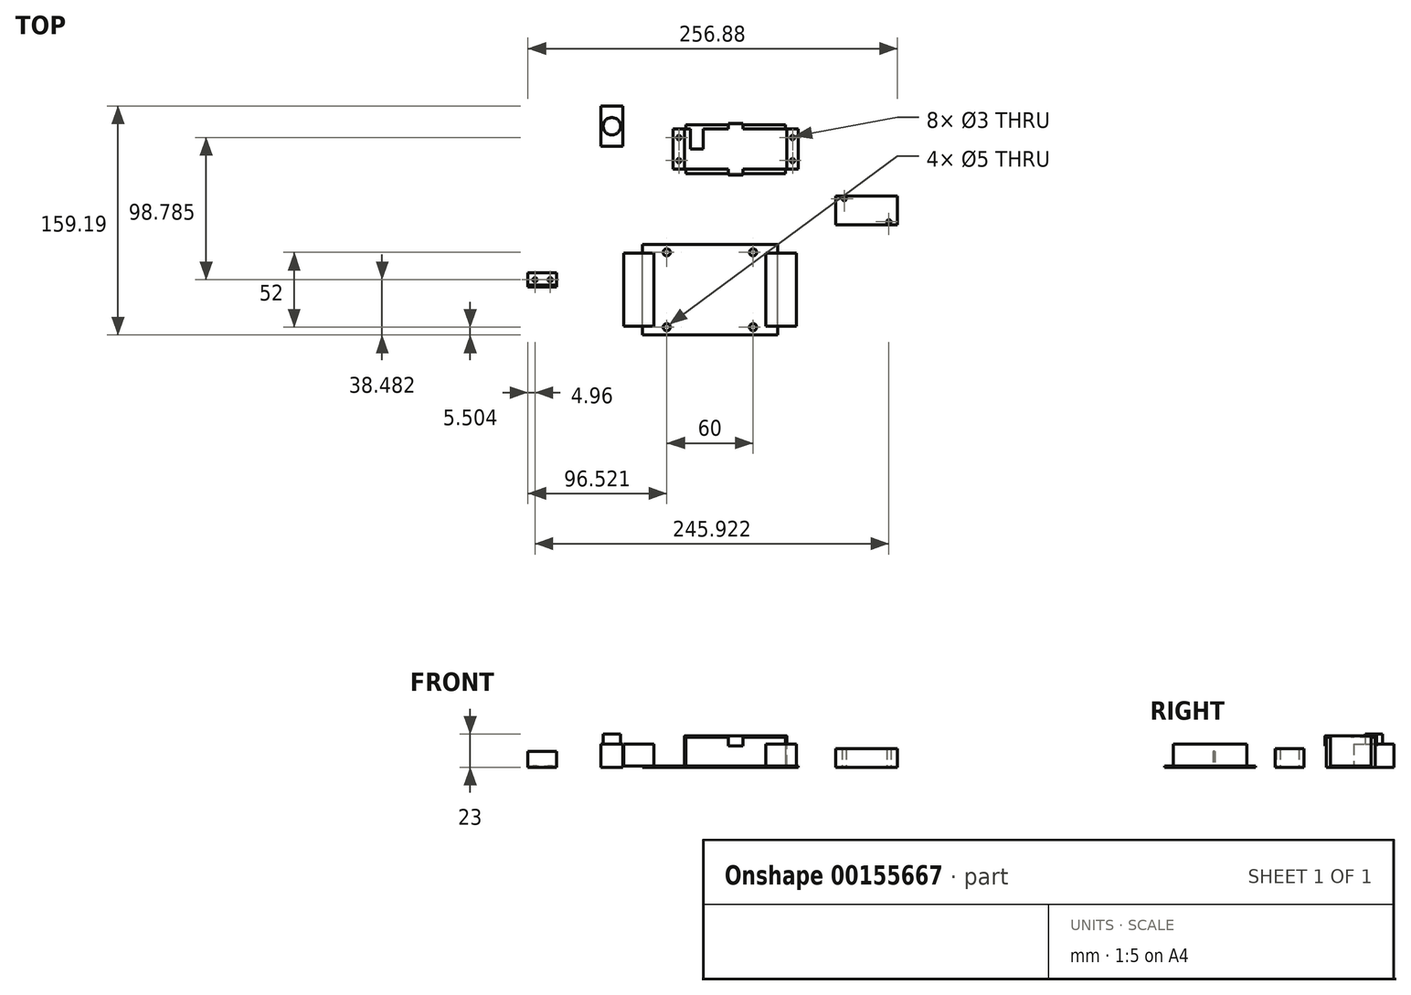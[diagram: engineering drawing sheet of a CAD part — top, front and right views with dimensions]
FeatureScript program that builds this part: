
annotation { "Feature Type Name" : "Feature", "Feature Type Description" : "" }
export const myFeature = defineFeature(function(context is Context, id is Id, definition is map)
    precondition{}
    {
        {
            var Q0;
            Q0=qCreatedBy(makeId("Top.planeOp"),FACE);
            var sketch = newSketch(context, id + "F0", { "sketchPlane" : qUnion([Q0])});
            skLineSegment(sketch, "E0.bottom", {"start": v(70.02, 20.44) * mm, "end": v(1.02, 20.44) * mm});
            skLineSegment(sketch, "E0.top", {"start": v(70.02, 54.44) * mm, "end": v(1.02, 54.44) * mm});
            skLineSegment(sketch, "E0.left", {"start": v(70.02, 20.44) * mm, "end": v(70.02, 54.44) * mm});
            skLineSegment(sketch, "E0.right", {"start": v(1.02, 20.44) * mm, "end": v(1.02, 54.44) * mm});
            skPoint(sketch, "E0.middle", {"position": v(35.52, 37.44) * mm});
            skSolve(sketch);
        }
        {
            var Q0;
            Q0 = qSketchRegion(id + "F0", true);
            extrude(context, id + "F1", {"entities" : qUnion([Q0]), "depth" : 21 * mm});
        }
        {
            var Q0;
            Q0=qCreatedBy(makeId("Top.planeOp"),FACE);
            var sketch = newSketch(context, id + "F2", { "sketchPlane" : qUnion([Q0])});
            skLineSegment(sketch, "E1.bottom", {"start": v(64.6, -91.83) * mm, "end": v(-29.4, -91.83) * mm});
            skLineSegment(sketch, "E1.top", {"start": v(64.6, -28.83) * mm, "end": v(-29.4, -28.83) * mm});
            skLineSegment(sketch, "E1.left", {"start": v(64.6, -91.83) * mm, "end": v(64.6, -28.83) * mm});
            skLineSegment(sketch, "E1.right", {"start": v(-29.4, -91.83) * mm, "end": v(-29.4, -28.83) * mm});
            skPoint(sketch, "E1.middle", {"position": v(17.6, -60.33) * mm});
            skCircle(sketch, "E2", {"center": v(-12.4, -86.33) * mm, "radius": 2.5 * mm});
            skCircle(sketch, "E3", {"center": v(-12.4, -34.33) * mm, "radius": 2.5 * mm});
            skCircle(sketch, "E4", {"center": v(47.6, -34.33) * mm, "radius": 2.5 * mm});
            skCircle(sketch, "E5", {"center": v(47.6, -86.33) * mm, "radius": 2.5 * mm});
            skSolve(sketch);
        }
        {
            var Q0;
            Q0 = qSketchRegion(id + "F2", true);
            extrude(context, id + "F3", {"entities" : qUnion([Q0]), "depth" : 1 * mm});
        }
        {
            var Q0;
            Q0=makeQuery(id+"F3.opExtrude","CAP_FACE",FACE,{"disambiguationData":[OSD([sQuery(id+"F2.wireOp",EDGE,"E1.bottom"),sQuery(id+"F2.wireOp",EDGE,"E1.top"),sQuery(id+"F2.wireOp",EDGE,"E1.left"),sQuery(id+"F2.wireOp",EDGE,"E1.right")])],"isStart":false});
            var sketch = newSketch(context, id + "F4", { "sketchPlane" : qUnion([Q0])});
            skLineSegment(sketch, "E6.bottom", {"start": v(-21.4, -85.83) * mm, "end": v(-42.4, -85.83) * mm});
            skLineSegment(sketch, "E6.top", {"start": v(-21.4, -34.83) * mm, "end": v(-42.4, -34.83) * mm});
            skLineSegment(sketch, "E6.left", {"start": v(-21.4, -85.83) * mm, "end": v(-21.4, -34.83) * mm});
            skLineSegment(sketch, "E6.right", {"start": v(-42.4, -85.83) * mm, "end": v(-42.4, -34.83) * mm});
            skPoint(sketch, "E6.middle", {"position": v(-31.9, -60.33) * mm});
            skPoint(sketch, "E7", {"position": v(-29.4, -60.33) * mm});
            skLineSegment(sketch, "E8.bottom", {"start": v(77.6, -85.83) * mm, "end": v(56.6, -85.83) * mm});
            skLineSegment(sketch, "E8.top", {"start": v(77.6, -34.83) * mm, "end": v(56.6, -34.83) * mm});
            skLineSegment(sketch, "E8.left", {"start": v(77.6, -85.83) * mm, "end": v(77.6, -34.83) * mm});
            skLineSegment(sketch, "E8.right", {"start": v(56.6, -85.83) * mm, "end": v(56.6, -34.83) * mm});
            skPoint(sketch, "E8.middle", {"position": v(67.1, -60.33) * mm});
            skPoint(sketch, "E8.middle.positionSnap0", {"position": v(64.6, -60.33) * mm});
            skPoint(sketch, "E8.centerSnap0", {"position": v(64.6, -60.33) * mm});
            skSolve(sketch);
        }
        {
            var Q0;
            Q0 = qSketchRegion(id + "F4", true);
            extrude(context, id + "F5", {"entities" : qUnion([Q0]), "operationType" : NewBodyOperationType.ADD, "depth" : 15 * mm});
        }
        {
            var Q0;
            Q0=qCreatedBy(makeId("Top.planeOp"),FACE);
            var sketch = newSketch(context, id + "F6", { "sketchPlane" : qUnion([Q0])});
            skLineSegment(sketch, "E9.bottom", {"start": v(147.95, -15.06) * mm, "end": v(104.95, -15.06) * mm});
            skLineSegment(sketch, "E9.top", {"start": v(147.95, 4.94) * mm, "end": v(104.95, 4.94) * mm});
            skLineSegment(sketch, "E9.left", {"start": v(147.95, -15.06) * mm, "end": v(147.95, 4.94) * mm});
            skLineSegment(sketch, "E9.right", {"start": v(104.95, -15.06) * mm, "end": v(104.95, 4.94) * mm});
            skPoint(sketch, "E9.middle", {"position": v(126.45, -5.06) * mm});
            skCircle(sketch, "E10", {"center": v(141.95, -13.06) * mm, "radius": 1.5 * mm});
            skCircle(sketch, "E11", {"center": v(110.95, 2.94) * mm, "radius": 1.5 * mm});
            skSolve(sketch);
        }
        {
            var Q0;
            Q0 = qSketchRegion(id + "F6", true);
            extrude(context, id + "F7", {"entities" : qUnion([Q0]), "depth" : 13 * mm});
        }
        {
            var Q0;
            Q0=qCreatedBy(makeId("Top.planeOp"),FACE);
            var sketch = newSketch(context, id + "F8", { "sketchPlane" : qUnion([Q0])});
            skLineSegment(sketch, "E12.bottom", {"start": v(-43.03, 39.36) * mm, "end": v(-58.03, 39.36) * mm});
            skLineSegment(sketch, "E12.top", {"start": v(-43.03, 67.36) * mm, "end": v(-58.03, 67.36) * mm});
            skLineSegment(sketch, "E12.left", {"start": v(-43.03, 39.36) * mm, "end": v(-43.03, 67.36) * mm});
            skLineSegment(sketch, "E12.right", {"start": v(-58.03, 39.36) * mm, "end": v(-58.03, 67.36) * mm});
            skPoint(sketch, "E12.middle", {"position": v(-50.53, 53.36) * mm});
            skSolve(sketch);
        }
        {
            var Q0;
            Q0 = qSketchRegion(id + "F8", true);
            extrude(context, id + "F9", {"entities" : qUnion([Q0]), "depth" : 16 * mm});
        }
        {
            var Q0;
            Q0=makeQuery(id+"F9.opExtrude","CAP_FACE",FACE,{"disambiguationData":[OSD([sQuery(id+"F8.wireOp",EDGE,"E12.bottom"),sQuery(id+"F8.wireOp",EDGE,"E12.top"),sQuery(id+"F8.wireOp",EDGE,"E12.left"),sQuery(id+"F8.wireOp",EDGE,"E12.right")])],"isStart":false});
            var sketch = newSketch(context, id + "F10", { "sketchPlane" : qUnion([Q0])});
            skCircle(sketch, "E13", {"center": v(-50.53, 53.36) * mm, "radius": 6 * mm});
            skSolve(sketch);
        }
        {
            var Q0;
            Q0 = qSketchRegion(id + "F10", true);
            extrude(context, id + "F11", {"entities" : qUnion([Q0]), "operationType" : NewBodyOperationType.ADD, "depth" : 7 * mm});
        }
        {
            var Q0;
            Q0=qCreatedBy(makeId("Top.planeOp"),FACE);
            var sketch = newSketch(context, id + "F12", { "sketchPlane" : qUnion([Q0])});
            skLineSegment(sketch, "E14.bottom", {"start": v(-108.93, -48.42) * mm, "end": v(-88.93, -48.42) * mm});
            skLineSegment(sketch, "E14.top", {"start": v(-108.93, -58.42) * mm, "end": v(-88.93, -58.42) * mm});
            skLineSegment(sketch, "E14.left", {"start": v(-108.93, -48.42) * mm, "end": v(-108.93, -58.42) * mm});
            skLineSegment(sketch, "E14.right", {"start": v(-88.93, -48.42) * mm, "end": v(-88.93, -58.42) * mm});
            skCircle(sketch, "E15", {"center": v(-103.97, -53.35) * mm, "radius": 1.5 * mm});
            skCircle(sketch, "E16", {"center": v(-93.43, -53.35) * mm, "radius": 1.5 * mm});
            skSolve(sketch);
        }
        {
            var Q0;
            Q0 = qSketchRegion(id + "F12", true);
            extrude(context, id + "F13", {"entities" : qUnion([Q0]), "depth" : 1 * mm});
        }
        {
            var Q0;
            Q0=makeQuery(id+"F13.opExtrude","CAP_FACE",FACE,{"disambiguationData":[OSD([sQuery(id+"F12.wireOp",EDGE,"E14.bottom"),sQuery(id+"F12.wireOp",EDGE,"E14.top"),sQuery(id+"F12.wireOp",EDGE,"E14.left"),sQuery(id+"F12.wireOp",EDGE,"E14.right"),sQuery(id+"F12.wireOp",EDGE,"E15"),sQuery(id+"F12.wireOp",EDGE,"E16")])],"isStart":false});
            var sketch = newSketch(context, id + "F14", { "sketchPlane" : qUnion([Q0])});
            skLineSegment(sketch, "E17.bottom", {"start": v(-108.93, -58.42) * mm, "end": v(-88.93, -58.42) * mm});
            skLineSegment(sketch, "E17.top", {"start": v(-108.93, -57.15) * mm, "end": v(-88.93, -57.15) * mm});
            skLineSegment(sketch, "E17.left", {"start": v(-108.93, -58.42) * mm, "end": v(-108.93, -57.15) * mm});
            skLineSegment(sketch, "E17.right", {"start": v(-88.93, -58.42) * mm, "end": v(-88.93, -57.15) * mm});
            skSolve(sketch);
        }
        {
            var Q0;
            Q0 = qSketchRegion(id + "F14", true);
            extrude(context, id + "F15", {"entities" : qUnion([Q0]), "operationType" : NewBodyOperationType.ADD, "depth" : 10 * mm});
        }
        {
            var Q0;
            Q0=makeQuery(id+"F1.opExtrude","CAP_FACE",FACE,{"disambiguationData":[OSD([sQuery(id+"F0.wireOp",EDGE,"E0.bottom"),sQuery(id+"F0.wireOp",EDGE,"E0.top"),sQuery(id+"F0.wireOp",EDGE,"E0.left"),sQuery(id+"F0.wireOp",EDGE,"E0.right")])],"isStart":false});
            var sketch = newSketch(context, id + "F16", { "sketchPlane" : qUnion([Q0])});
            skLineSegment(sketch, "E18.bottom", {"start": v(1.02, 51.44) * mm, "end": v(4.02, 51.44) * mm});
            skLineSegment(sketch, "E18.top", {"start": v(1.02, 23.44) * mm, "end": v(70.02, 23.44) * mm});
            skLineSegment(sketch, "E18.left", {"start": v(1.02, 51.44) * mm, "end": v(1.02, 23.44) * mm});
            skLineSegment(sketch, "E18.right", {"start": v(70.02, 51.44) * mm, "end": v(70.02, 23.44) * mm});
            skLineSegment(sketch, "E19.top", {"start": v(4.02, 37.44) * mm, "end": v(13.02, 37.44) * mm});
            skLineSegment(sketch, "E19.left", {"start": v(4.02, 51.44) * mm, "end": v(4.02, 37.44) * mm});
            skLineSegment(sketch, "E19.right", {"start": v(13.02, 51.44) * mm, "end": v(13.02, 37.44) * mm});
            skLineSegment(sketch, "E20.trimOffspring", {"start": v(13.02, 51.44) * mm, "end": v(70.02, 51.44) * mm});
            skLineSegment(sketch, "E21.bottom", {"start": v(30.52, 23.44) * mm, "end": v(40.52, 23.44) * mm});
            skLineSegment(sketch, "E21.top", {"start": v(30.52, 20.44) * mm, "end": v(40.52, 20.44) * mm});
            skLineSegment(sketch, "E21.left", {"start": v(30.52, 23.44) * mm, "end": v(30.52, 20.44) * mm});
            skLineSegment(sketch, "E21.right", {"start": v(40.52, 23.44) * mm, "end": v(40.52, 20.44) * mm});
            skLineSegment(sketch, "E22.bottom", {"start": v(30.52, 51.44) * mm, "end": v(40.52, 51.44) * mm});
            skLineSegment(sketch, "E22.top", {"start": v(30.52, 54.44) * mm, "end": v(40.52, 54.44) * mm});
            skLineSegment(sketch, "E22.left", {"start": v(30.52, 51.44) * mm, "end": v(30.52, 54.44) * mm});
            skLineSegment(sketch, "E22.right", {"start": v(40.52, 51.44) * mm, "end": v(40.52, 54.44) * mm});
            skSolve(sketch);
        }
        {
            var Q0;
            Q0 = qSketchRegion(id + "F16", true);
            extrude(context, id + "F17", {"entities" : qUnion([Q0]), "depth" : 1 * mm});
        }
        {
            var Q0;
            Q0=makeQuery(id+"F17.opExtrude","CAP_FACE",FACE,{"disambiguationData":[OSD([sQuery(id+"F16.wireOp",EDGE,"E18.bottom"),sQuery(id+"F16.wireOp",EDGE,"E18.top"),sQuery(id+"F16.wireOp",EDGE,"E18.left"),sQuery(id+"F16.wireOp",EDGE,"E18.right")])],"isStart":false});
            var sketch = newSketch(context, id + "F18", { "sketchPlane" : qUnion([Q0])});
            skLineSegment(sketch, "E23.bottom", {"start": v(1.02, 51.44) * mm, "end": v(0.02, 51.44) * mm});
            skLineSegment(sketch, "E23.top", {"start": v(1.02, 23.44) * mm, "end": v(0.02, 23.44) * mm});
            skLineSegment(sketch, "E23.left", {"start": v(1.02, 51.44) * mm, "end": v(1.02, 23.44) * mm});
            skLineSegment(sketch, "E23.right", {"start": v(0.02, 51.44) * mm, "end": v(0.02, 23.44) * mm});
            skLineSegment(sketch, "E24.bottom", {"start": v(70.02, 51.44) * mm, "end": v(71.02, 51.44) * mm});
            skLineSegment(sketch, "E24.top", {"start": v(70.02, 23.44) * mm, "end": v(71.02, 23.44) * mm});
            skLineSegment(sketch, "E24.left", {"start": v(70.02, 51.44) * mm, "end": v(70.02, 23.44) * mm});
            skLineSegment(sketch, "E24.right", {"start": v(71.02, 51.44) * mm, "end": v(71.02, 23.44) * mm});
            skLineSegment(sketch, "E25.bottom", {"start": v(30.52, 20.44) * mm, "end": v(40.52, 20.44) * mm});
            skLineSegment(sketch, "E25.top", {"start": v(30.52, 19.44) * mm, "end": v(40.52, 19.44) * mm});
            skLineSegment(sketch, "E25.left", {"start": v(30.52, 20.44) * mm, "end": v(30.52, 19.44) * mm});
            skLineSegment(sketch, "E25.right", {"start": v(40.52, 20.44) * mm, "end": v(40.52, 19.44) * mm});
            skLineSegment(sketch, "E26.bottom", {"start": v(30.52, 54.44) * mm, "end": v(40.52, 54.44) * mm});
            skLineSegment(sketch, "E26.top", {"start": v(30.52, 55.44) * mm, "end": v(40.52, 55.44) * mm});
            skLineSegment(sketch, "E26.left", {"start": v(30.52, 54.44) * mm, "end": v(30.52, 55.44) * mm});
            skLineSegment(sketch, "E26.right", {"start": v(40.52, 54.44) * mm, "end": v(40.52, 55.44) * mm});
            skSolve(sketch);
        }
        {
            var Q0;
            Q0=makeQuery(id+"F18.imprint","IMPRINT",FACE,{"disambiguationData":[TD([[makeQuery(id+"F18.imprint","IMPRINT",EDGE,{"derivedFrom":sQuery(id+"F18.wireOp",EDGE,"E23.bottom")}),1.0]])]});
            var Q1;
            Q1=makeQuery(id+"F18.imprint","IMPRINT",FACE,{"disambiguationData":[TD([[makeQuery(id+"F18.imprint","IMPRINT",EDGE,{"derivedFrom":sQuery(id+"F18.wireOp",EDGE,"E24.bottom")}),-1.0]])]});
            extrude(context, id + "F19", {"entities" : qUnion([Q0, Q1]), "operationType" : NewBodyOperationType.ADD, "oppositeDirection" : true, "depth" : 22 * mm});
        }
        {
            var Q0;
            Q0=makeQuery(id+"F19.opExtrude","SWEPT_FACE",FACE,{"disambiguationData":[OSD([sQuery(id+"F18.wireOp",EDGE,"E23.right")])]});
            var sketch = newSketch(context, id + "F20", { "sketchPlane" : qUnion([Q0])});
            skLineSegment(sketch, "E27.bottom", {"start": v(-51.44, 0) * mm, "end": v(-23.44, 0) * mm});
            skLineSegment(sketch, "E27.top", {"start": v(-51.44, 1) * mm, "end": v(-23.44, 1) * mm});
            skLineSegment(sketch, "E27.left", {"start": v(-51.44, 0) * mm, "end": v(-51.44, 1) * mm});
            skLineSegment(sketch, "E27.right", {"start": v(-23.44, 0) * mm, "end": v(-23.44, 1) * mm});
            skSolve(sketch);
        }
        {
            var Q0;
            Q0 = qSketchRegion(id + "F20", true);
            extrude(context, id + "F21", {"entities" : qUnion([Q0]), "operationType" : NewBodyOperationType.ADD, "depth" : 8 * mm});
        }
        {
            var Q0;
            Q0=makeQuery(id+"F19.opExtrude","SWEPT_FACE",FACE,{"disambiguationData":[OSD([sQuery(id+"F18.wireOp",EDGE,"E24.right")])]});
            var sketch = newSketch(context, id + "F22", { "sketchPlane" : qUnion([Q0])});
            skLineSegment(sketch, "E28.bottom", {"start": v(23.44, 0) * mm, "end": v(51.44, 0) * mm});
            skLineSegment(sketch, "E28.top", {"start": v(23.44, 1) * mm, "end": v(51.44, 1) * mm});
            skLineSegment(sketch, "E28.left", {"start": v(23.44, 0) * mm, "end": v(23.44, 1) * mm});
            skLineSegment(sketch, "E28.right", {"start": v(51.44, 0) * mm, "end": v(51.44, 1) * mm});
            skSolve(sketch);
        }
        {
            var Q0;
            Q0 = qSketchRegion(id + "F22", true);
            extrude(context, id + "F23", {"entities" : qUnion([Q0]), "operationType" : NewBodyOperationType.ADD, "depth" : 8 * mm});
        }
        {
            var Q0;
            Q0=makeQuery(id+"F21.opExtrude","SWEPT_FACE",FACE,{"disambiguationData":[OSD([sQuery(id+"F20.wireOp",EDGE,"E27.top")])]});
            var sketch = newSketch(context, id + "F24", { "sketchPlane" : qUnion([Q0])});
            skCircle(sketch, "E29", {"center": v(-3.98, 45.44) * mm, "radius": 1.5 * mm});
            skCircle(sketch, "E30", {"center": v(-3.98, 29.44) * mm, "radius": 1.5 * mm});
            skPoint(sketch, "E31", {"position": v(-3.98, 51.44) * mm});
            skCircle(sketch, "E32", {"center": v(75.02, 45.44) * mm, "radius": 1.5 * mm});
            skCircle(sketch, "E33", {"center": v(75.02, 29.44) * mm, "radius": 1.5 * mm});
            skSolve(sketch);
        }
        {
            var Q0;
            Q0 = qSketchRegion(id + "F24", true);
            extrude(context, id + "F25", {"entities" : qUnion([Q0]), "operationType" : NewBodyOperationType.REMOVE, "oppositeDirection" : true, "depth" : 1 * mm});
        }
        {
            var Q0;
            Q0=makeQuery(id+"F18.imprint","IMPRINT",FACE,{"disambiguationData":[TD([[makeQuery(id+"F18.imprint","IMPRINT",EDGE,{"derivedFrom":sQuery(id+"F18.wireOp",EDGE,"E26.bottom")}),-1.0]])]});
            var Q1;
            Q1=makeQuery(id+"F18.imprint","IMPRINT",FACE,{"disambiguationData":[TD([[makeQuery(id+"F18.imprint","IMPRINT",EDGE,{"derivedFrom":sQuery(id+"F18.wireOp",EDGE,"E25.bottom")}),1.0]])]});
            extrude(context, id + "F26", {"entities" : qUnion([Q0, Q1]), "operationType" : NewBodyOperationType.ADD, "oppositeDirection" : true, "depth" : 7 * mm});
        }
        {
            var Q0;
            Q0=makeQuery(id+"F23.opExtrude","CAP_EDGE",EDGE,{"disambiguationData":[OSD([sQuery(id+"F22.wireOp",EDGE,"E28.top")])],"isStart":true});
            var Q1;
            Q1=makeQuery(id+"F19.opExtrude","CAP_EDGE",EDGE,{"disambiguationData":[OSD([sQuery(id+"F18.wireOp",EDGE,"E24.right")])],"isStart":true});
            var Q2;
            Q2=makeQuery(id+"F26.opExtrude","CAP_EDGE",EDGE,{"disambiguationData":[OSD([sQuery(id+"F18.wireOp",EDGE,"E25.top")])],"isStart":true});
            var Q3;
            Q3=makeQuery(id+"F26.opExtrude","CAP_EDGE",EDGE,{"disambiguationData":[OSD([sQuery(id+"F18.wireOp",EDGE,"E26.top")])],"isStart":true});
            var Q4;
            Q4=makeQuery(id+"F19.opExtrude","CAP_EDGE",EDGE,{"disambiguationData":[OSD([sQuery(id+"F18.wireOp",EDGE,"E23.right")])],"isStart":true});
            var Q5;
            Q5=makeQuery(id+"F21.opExtrude","CAP_EDGE",EDGE,{"disambiguationData":[OSD([sQuery(id+"F20.wireOp",EDGE,"E27.top")])],"isStart":true});
            var Q6;
            Q6=makeQuery(id+"F19.opExtrude","CAP_EDGE",EDGE,{"disambiguationData":[OSD([sQuery(id+"F18.wireOp",EDGE,"E24.left")])],"isStart":false});
            var Q7;
            Q7=makeQuery(id+"F17.opExtrude","CAP_EDGE",EDGE,{"disambiguationData":[OSD([sQuery(id+"F16.wireOp",EDGE,"E18.right")])],"isStart":true});
            var Q8;
            Q8=makeQuery(id+"F17.opExtrude","CAP_EDGE",EDGE,{"disambiguationData":[OSD([sQuery(id+"F16.wireOp",EDGE,"E22.top")])],"isStart":true});
            var Q9;
            Q9=makeQuery(id+"F17.opExtrude","CAP_EDGE",EDGE,{"disambiguationData":[OSD([sQuery(id+"F16.wireOp",EDGE,"E21.top")])],"isStart":true});
            var Q10;
            Q10=makeQuery(id+"F17.opExtrude","CAP_EDGE",EDGE,{"disambiguationData":[OSD([sQuery(id+"F16.wireOp",EDGE,"E18.left")])],"isStart":true});
            var Q11;
            Q11=makeQuery(id+"F19.opExtrude","CAP_EDGE",EDGE,{"disambiguationData":[OSD([sQuery(id+"F18.wireOp",EDGE,"E23.left")])],"isStart":false});
            fillet(context, id + "F27", {"entities" : qUnion([Q0, Q1, Q2, Q3, Q4, Q5, Q6, Q7, Q8, Q9, Q10, Q11]), "radius" : 0.5 * mm, "tangentPropagation" : true, "allowEdgeOverflow" : false});
        }
    });
